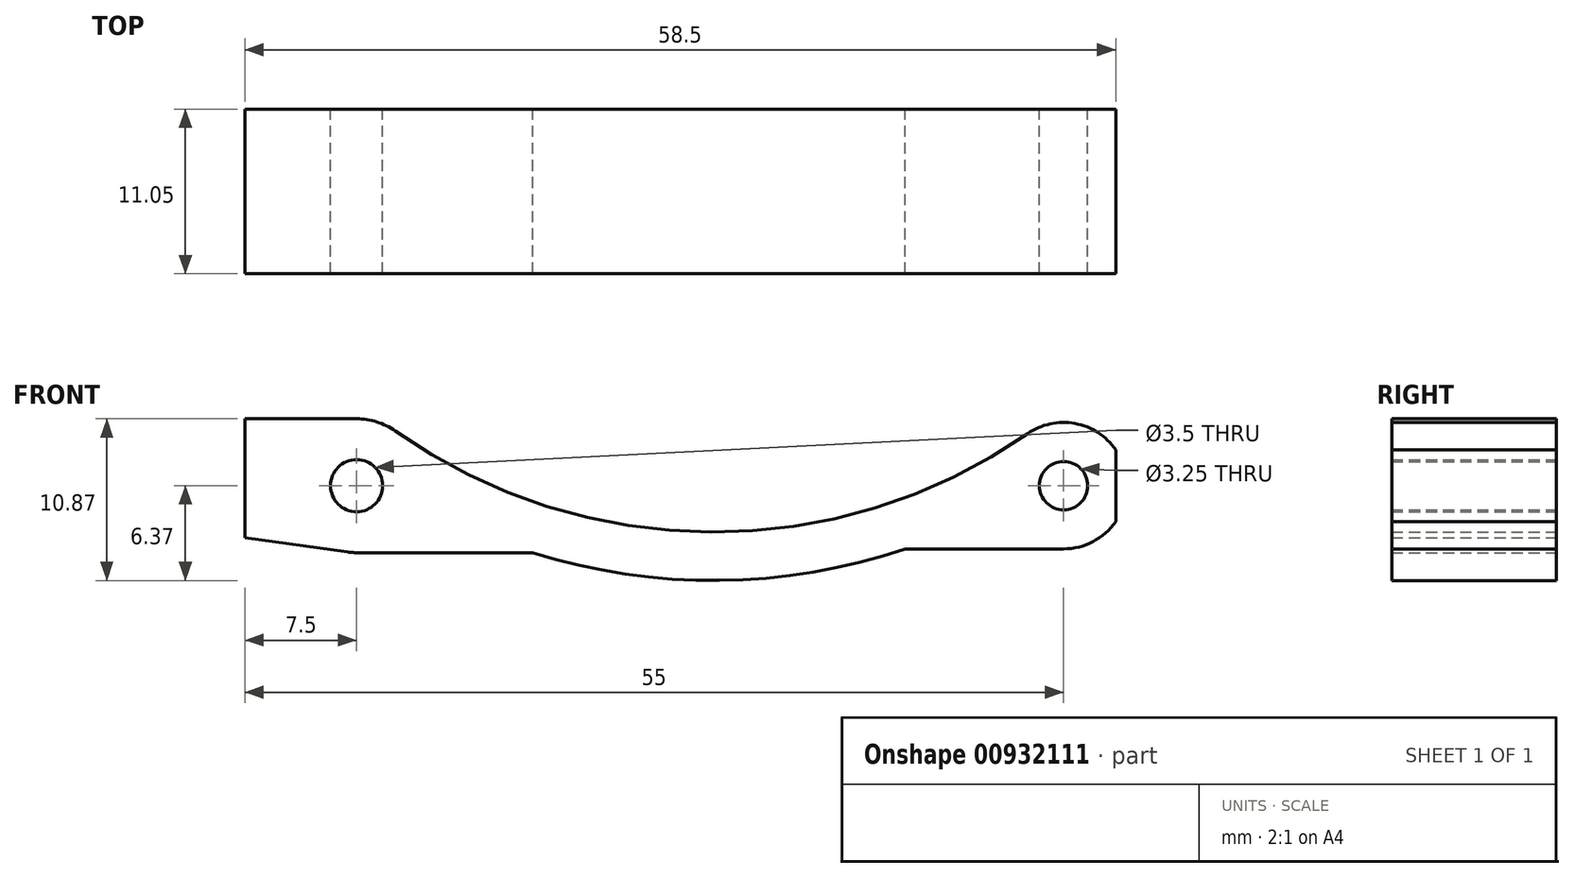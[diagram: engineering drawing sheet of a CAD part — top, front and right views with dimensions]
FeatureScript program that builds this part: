
annotation { "Feature Type Name" : "Feature", "Feature Type Description" : "" }
export const myFeature = defineFeature(function(context is Context, id is Id, definition is map)
    precondition{}
    {
        {
            var Q0;
            Q0=qCreatedBy(makeId("Front.planeOp"),FACE);
            var sketch = newSketch(context, id + "F0", { "sketchPlane" : qUnion([Q0])});
            skLineSegment(sketch, "E0", {"start": v(0, 0) * mm, "end": v(47.5, 0) * mm, "construction": true});
            skCircle(sketch, "E1", {"center": v(0, 0) * mm, "radius": 1.75 * mm});
            skCircle(sketch, "E2", {"center": v(47.5, 0) * mm, "radius": 1.63 * mm});
            skArc(sketch, "E3", {"start": v(-0.62, -4.46) * mm, "mid": v(-0.31, -4.49) * mm, "end": v(0, -4.5) * mm});
            skArc(sketch, "E4", {"start": v(47.5, -4.25) * mm, "mid": v(49.48, -3.76) * mm, "end": v(51, -2.41) * mm});
            skArc(sketch, "E5", {"start": v(2.6, 3.67) * mm, "mid": v(23.8, -3.12) * mm, "end": v(45.08, 3.5) * mm});
            skLineSegment(sketch, "E6", {"start": v(0, -4.5) * mm, "end": v(11.84, -4.5) * mm});
            skLineSegment(sketch, "E7", {"start": v(-7.5, -3.5) * mm, "end": v(-7.5, 4.5) * mm});
            skLineSegment(sketch, "E8", {"start": v(-7.5, 4.5) * mm, "end": v(0, 4.5) * mm});
            skArc(sketch, "E9.trimOffspring", {"start": v(11.84, -4.5) * mm, "mid": v(24.37, -6.37) * mm, "end": v(36.86, -4.25) * mm});
            skLineSegment(sketch, "E10", {"start": v(-7.5, -3.5) * mm, "end": v(-0.62, -4.46) * mm});
            skArc(sketch, "E11.trimOffspring", {"start": v(2.6, 3.67) * mm, "mid": v(1.36, 4.29) * mm, "end": v(0, 4.5) * mm});
            skLineSegment(sketch, "E12", {"start": v(36.86, -4.25) * mm, "end": v(47.5, -4.25) * mm});
            skLineSegment(sketch, "E13", {"start": v(51, 2.41) * mm, "end": v(51, -2.41) * mm});
            skArc(sketch, "E14.trimOffspring", {"start": v(51, 2.41) * mm, "mid": v(48.26, 4.18) * mm, "end": v(45.08, 3.5) * mm});
            skSolve(sketch);
        }
        {
            var Q0;
            Q0 = qSketchRegion(id + "F0", true);
            extrude(context, id + "F1", {"entities" : qUnion([Q0]), "depth" : 11.05 * mm, "offsetDistance" : 25 * mm});
        }
    });
